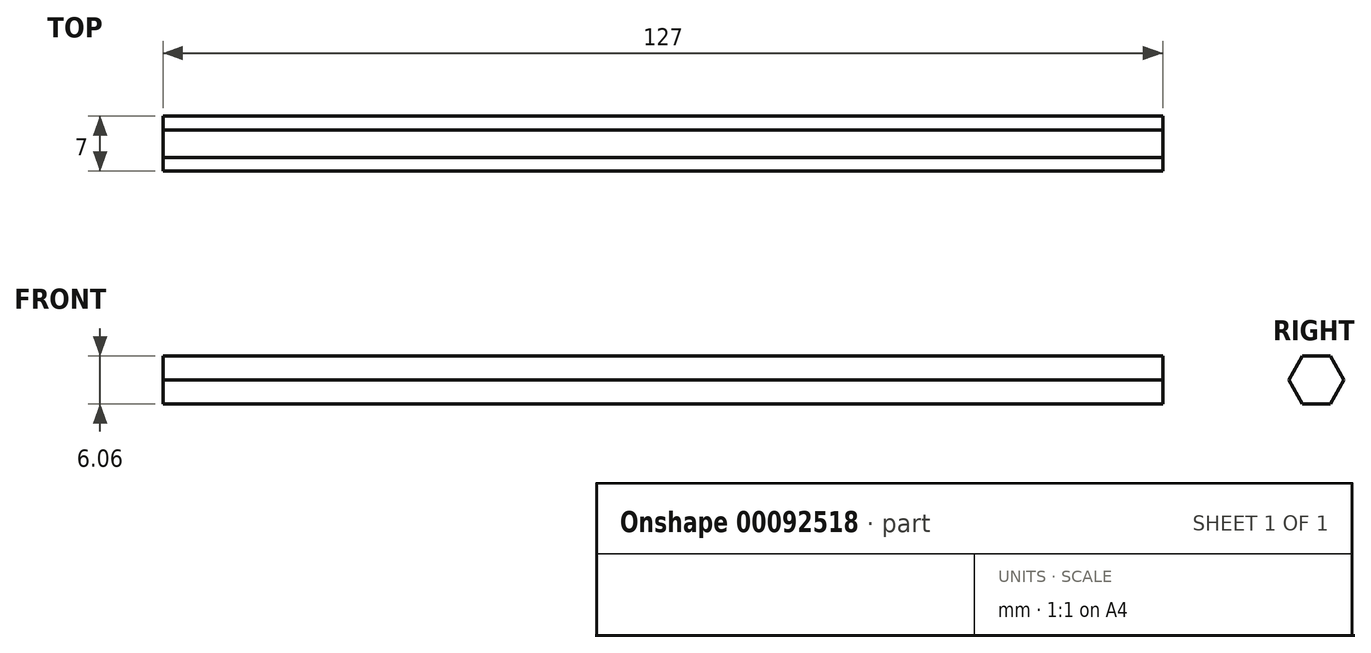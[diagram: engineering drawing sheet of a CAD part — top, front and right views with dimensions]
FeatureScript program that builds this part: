
annotation { "Feature Type Name" : "Feature", "Feature Type Description" : "" }
export const myFeature = defineFeature(function(context is Context, id is Id, definition is map)
    precondition{}
    {
        {
            var Q0;
            Q0=qCreatedBy(makeId("Right.planeOp"),FACE);
            var sketch = newSketch(context, id + "F0", { "sketchPlane" : qUnion([Q0])});
            skCircle(sketch, "E0.cCircle", {"center": v(0, 0) * mm, "radius": 3.5 * mm, "construction": true});
            skLineSegment(sketch, "E0.0", {"start": v(-3.5, 0) * mm, "end": v(-1.75, 3.03) * mm});
            skLineSegment(sketch, "E0.1", {"start": v(-1.75, 3.03) * mm, "end": v(1.75, 3.03) * mm});
            skLineSegment(sketch, "E0.2", {"start": v(1.75, 3.03) * mm, "end": v(3.5, 0) * mm});
            skLineSegment(sketch, "E0.3", {"start": v(3.5, 0) * mm, "end": v(1.75, -3.03) * mm});
            skLineSegment(sketch, "E0.4", {"start": v(1.75, -3.03) * mm, "end": v(-1.75, -3.03) * mm});
            skLineSegment(sketch, "E0.5", {"start": v(-1.75, -3.03) * mm, "end": v(-3.5, 0) * mm});
            skSolve(sketch);
        }
        {
            var Q0;
            Q0=makeQuery(id+"F0.imprint","IMPRINT",FACE,{"disambiguationData":[TD([[makeQuery(id+"F0.imprint","IMPRINT",EDGE,{"derivedFrom":sQuery(id+"F0.wireOp",EDGE,"E0.0")}),-1.0]])]});
            extrude(context, id + "F1", {"entities" : qUnion([Q0]), "depth" : 127 * mm});
        }
    });
